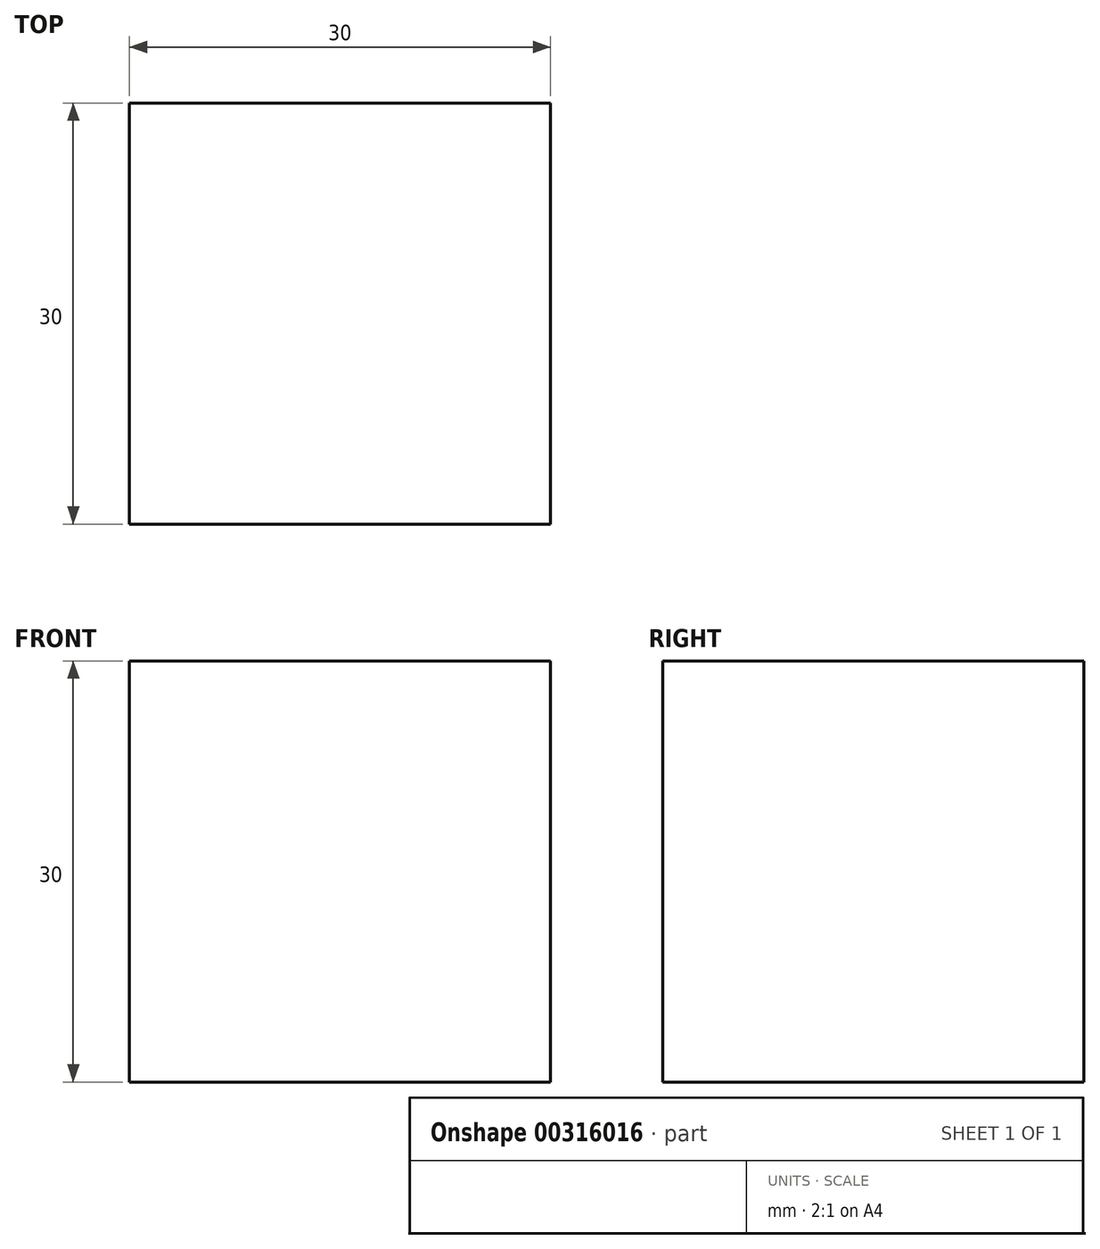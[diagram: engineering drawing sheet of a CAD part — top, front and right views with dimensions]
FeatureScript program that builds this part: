
annotation { "Feature Type Name" : "Feature", "Feature Type Description" : "" }
export const myFeature = defineFeature(function(context is Context, id is Id, definition is map)
    precondition{}
    {
        {
            var Q0;
            Q0=qCreatedBy(makeId("Top.planeOp"),FACE);
            var sketch = newSketch(context, id + "F0", { "sketchPlane" : qUnion([Q0])});
            skLineSegment(sketch, "E0.bottom", {"start": v(-15, 15) * mm, "end": v(15, 15) * mm});
            skLineSegment(sketch, "E0.top", {"start": v(-15, -15) * mm, "end": v(15, -15) * mm});
            skLineSegment(sketch, "E0.left", {"start": v(-15, 15) * mm, "end": v(-15, -15) * mm});
            skLineSegment(sketch, "E0.right", {"start": v(15, 15) * mm, "end": v(15, -15) * mm});
            skPoint(sketch, "E0.middle", {"position": v(0, 0) * mm});
            skSolve(sketch);
        }
        {
            var Q0;
            Q0=makeQuery(id+"F0.imprint","IMPRINT",FACE,{"disambiguationData":[TD([[makeQuery(id+"F0.imprint","IMPRINT",EDGE,{"derivedFrom":sQuery(id+"F0.wireOp",EDGE,"E0.bottom")}),-1.0]])]});
            extrude(context, id + "F1", {"entities" : qUnion([Q0]), "depth" : 30 * mm, "offsetDistance" : 25 * mm});
        }
    });
